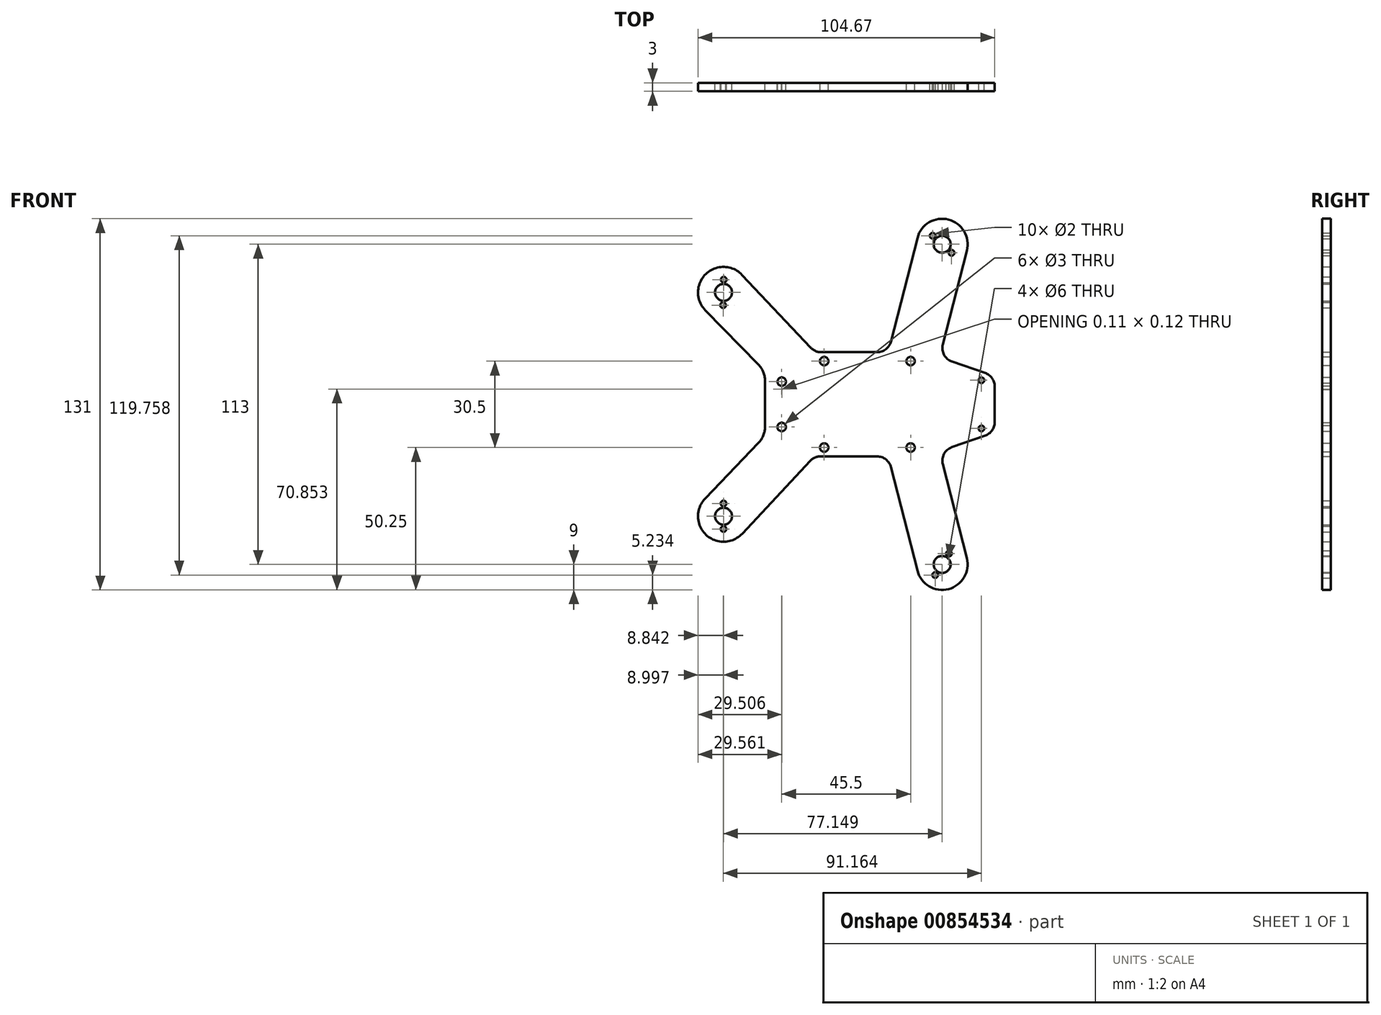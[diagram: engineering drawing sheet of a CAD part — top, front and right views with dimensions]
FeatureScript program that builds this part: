
annotation { "Feature Type Name" : "Feature", "Feature Type Description" : "" }
export const myFeature = defineFeature(function(context is Context, id is Id, definition is map)
    precondition{}
    {
        {
            var Q0;
            Q0=qCreatedBy(makeId("Front.planeOp"),FACE);
            var sketch = newSketch(context, id + "F0", { "sketchPlane" : qUnion([Q0])});
            skLineSegment(sketch, "E0.bottom", {"start": v(-3.88, -18.39) * mm, "end": v(-23.86, -18.39) * mm});
            skLineSegment(sketch, "E0.top", {"start": v(-3.88, 18.39) * mm, "end": v(-23.64, 18.39) * mm});
            skLineSegment(sketch, "E0.left", {"start": v(37.58, -6.33) * mm, "end": v(37.58, -5.89) * mm});
            skLineSegment(sketch, "E0.right", {"start": v(-37.58, -5.3) * mm, "end": v(-37.58, 5.3) * mm});
            skPoint(sketch, "E0.middle", {"position": v(0, 0) * mm});
            skPoint(sketch, "E1", {"position": v(-22.58, 15.25) * mm});
            skPoint(sketch, "E2", {"position": v(-22.58, -15.25) * mm});
            skPoint(sketch, "E3", {"position": v(7.92, 15.25) * mm});
            skPoint(sketch, "E4", {"position": v(7.92, -15.25) * mm});
            skPoint(sketch, "E5", {"position": v(32.92, 8.5) * mm});
            skPoint(sketch, "E6", {"position": v(32.92, -8.5) * mm});
            skCircle(sketch, "E7", {"center": v(-22.58, 15.25) * mm, "radius": 1.5 * mm});
            skCircle(sketch, "E8", {"center": v(-22.58, -15.25) * mm, "radius": 1.5 * mm});
            skCircle(sketch, "E9", {"center": v(7.92, 15.25) * mm, "radius": 1.5 * mm});
            skCircle(sketch, "E10", {"center": v(7.92, -15.25) * mm, "radius": 1.5 * mm});
            skCircle(sketch, "E11", {"center": v(32.92, 8.5) * mm, "radius": 1 * mm});
            skCircle(sketch, "E12", {"center": v(32.92, -8.5) * mm, "radius": 1 * mm});
            skArc(sketch, "E13", {"start": v(-37.47, 5.41) * mm, "mid": v(-37.53, 5.35) * mm, "end": v(-37.58, 5.3) * mm});
            skLineSegment(sketch, "E14", {"start": v(-37.47, 5.41) * mm, "end": v(-37.58, 5.3) * mm});
            skPoint(sketch, "E15.orphan", {"position": v(-37.58, 18.39) * mm});
            skPoint(sketch, "E16.orphan", {"position": v(-37.58, -18.39) * mm});
            skPoint(sketch, "E17", {"position": v(37.58, -9.89) * mm});
            skPoint(sketch, "E18", {"position": v(37.58, 9.89) * mm});
            skLineSegment(sketch, "E19", {"start": v(22.48, 15.14) * mm, "end": v(34.23, 11.05) * mm});
            skLineSegment(sketch, "E20", {"start": v(22.48, -15.14) * mm, "end": v(34.23, -11.05) * mm});
            skPoint(sketch, "E21.orphan", {"position": v(37.58, 18.39) * mm});
            skPoint(sketch, "E22.orphan", {"position": v(37.58, -18.39) * mm});
            skPoint(sketch, "E23", {"position": v(37.58, 5.89) * mm});
            skPoint(sketch, "E24", {"position": v(37.58, -5.89) * mm});
            skLineSegment(sketch, "E25.trimOffspring", {"start": v(37.58, 5.89) * mm, "end": v(37.58, 6.33) * mm});
            skPoint(sketch, "E26", {"position": v(-58.1, 39.5) * mm});
            skPoint(sketch, "E27", {"position": v(-58.1, -39.5) * mm});
            skPoint(sketch, "E28", {"position": v(19.06, -56.5) * mm});
            skPoint(sketch, "E29", {"position": v(19.06, 56.5) * mm});
            skPoint(sketch, "E30.center.orphan", {"position": v(-19.86, 0) * mm});
            skPoint(sketch, "E31.center.orphan", {"position": v(23.9, 0) * mm});
            skLineSegment(sketch, "E32", {"start": v(37.58, 5.89) * mm, "end": v(37.58, -5.89) * mm});
            skCircle(sketch, "E33", {"center": v(-58.1, -39.5) * mm, "radius": 3 * mm});
            skCircle(sketch, "E34", {"center": v(-58.1, 39.5) * mm, "radius": 3 * mm});
            skCircle(sketch, "E35", {"center": v(19.06, 56.5) * mm, "radius": 3 * mm});
            skCircle(sketch, "E36", {"center": v(19.06, -56.5) * mm, "radius": 3 * mm});
            skArc(sketch, "E37", {"start": v(-64.59, -33.27) * mm, "mid": v(-64.28, -46.03) * mm, "end": v(-51.52, -45.65) * mm});
            skArc(sketch, "E38", {"start": v(10.34, -58.73) * mm, "mid": v(21.29, -65.22) * mm, "end": v(27.77, -54.27) * mm});
            skArc(sketch, "E39", {"start": v(-51.55, 45.68) * mm, "mid": v(-64.33, 46) * mm, "end": v(-64.53, 33.21) * mm});
            skArc(sketch, "E40", {"start": v(27.77, 54.27) * mm, "mid": v(21.29, 65.22) * mm, "end": v(10.34, 58.73) * mm});
            skLineSegment(sketch, "E41", {"start": v(-45.75, 13.98) * mm, "end": v(-64.53, 33.21) * mm});
            skLineSegment(sketch, "E42", {"start": v(-27.27, 19.96) * mm, "end": v(-51.55, 45.68) * mm});
            skLineSegment(sketch, "E43", {"start": v(-27.52, -19.97) * mm, "end": v(-51.52, -45.65) * mm});
            skLineSegment(sketch, "E44", {"start": v(-45.7, -13.58) * mm, "end": v(-64.59, -33.27) * mm});
            skLineSegment(sketch, "E45", {"start": v(27.77, 54.27) * mm, "end": v(19.28, 21.1) * mm});
            skLineSegment(sketch, "E46", {"start": v(19.28, -21.1) * mm, "end": v(27.77, -54.27) * mm});
            skLineSegment(sketch, "E47", {"start": v(0.96, -22.15) * mm, "end": v(10.34, -58.73) * mm});
            skLineSegment(sketch, "E48", {"start": v(0.96, 22.15) * mm, "end": v(10.34, 58.73) * mm});
            skLineSegment(sketch, "E49", {"start": v(-43.47, 8.4) * mm, "end": v(-43.47, -8.04) * mm});
            skPoint(sketch, "E50.newPointA", {"position": v(13.14, -18.39) * mm});
            skPoint(sketch, "E50.newPointB", {"position": v(0, -18.39) * mm});
            skArc(sketch, "E50.filletArc", {"start": v(0.96, -22.15) * mm, "mid": v(-0.81, -19.44) * mm, "end": v(-3.88, -18.39) * mm});
            skPoint(sketch, "E51.newPointA", {"position": v(0, 18.39) * mm});
            skPoint(sketch, "E51.newPointB", {"position": v(13.14, 18.39) * mm});
            skArc(sketch, "E51.filletArc", {"start": v(-3.88, 18.39) * mm, "mid": v(-0.81, 19.44) * mm, "end": v(0.96, 22.15) * mm});
            skPoint(sketch, "E52.visualSharp", {"position": v(-25.8, 18.39) * mm});
            skArc(sketch, "E52.filletArc", {"start": v(-27.27, 19.96) * mm, "mid": v(-25.62, 18.8) * mm, "end": v(-23.64, 18.39) * mm});
            skPoint(sketch, "E53.visualSharp", {"position": v(-26.03, -18.39) * mm});
            skArc(sketch, "E53.filletArc", {"start": v(-23.86, -18.39) * mm, "mid": v(-25.85, -18.8) * mm, "end": v(-27.52, -19.97) * mm});
            skArc(sketch, "E54.filletArc", {"start": v(-45.7, -13.58) * mm, "mid": v(-44.05, -11.02) * mm, "end": v(-43.47, -8.04) * mm});
            skArc(sketch, "E55.filletArc", {"start": v(-43.47, 8.4) * mm, "mid": v(-44.06, 11.41) * mm, "end": v(-45.75, 13.98) * mm});
            skPoint(sketch, "E56.newPointA", {"position": v(18.14, 16.65) * mm});
            skArc(sketch, "E56.filletArc", {"start": v(19.28, 21.1) * mm, "mid": v(19.72, 17.5) * mm, "end": v(22.48, 15.14) * mm});
            skPoint(sketch, "E57.newPointB", {"position": v(18.14, -16.65) * mm});
            skArc(sketch, "E57.filletArc", {"start": v(22.48, -15.14) * mm, "mid": v(19.72, -17.5) * mm, "end": v(19.28, -21.1) * mm});
            skArc(sketch, "E58.filletArc", {"start": v(34.23, -11.05) * mm, "mid": v(36.66, -9.23) * mm, "end": v(37.58, -6.33) * mm});
            skArc(sketch, "E59.filletArc", {"start": v(37.58, 6.33) * mm, "mid": v(36.66, 9.23) * mm, "end": v(34.23, 11.05) * mm});
            skLineSegment(sketch, "E60", {"start": v(-37.56, 8) * mm, "end": v(-37.56, 0) * mm});
            skLineSegment(sketch, "E61", {"start": v(-37.56, 0) * mm, "end": v(-37.58, -8) * mm});
            skCircle(sketch, "E62", {"center": v(-37.56, 8) * mm, "radius": 1.5 * mm});
            skCircle(sketch, "E63", {"center": v(-37.58, -8) * mm, "radius": 1.5 * mm});
            skCircle(sketch, "E64", {"center": v(-58.02, 44) * mm, "radius": 1 * mm});
            skCircle(sketch, "E65", {"center": v(-58.25, 35) * mm, "radius": 1 * mm});
            skCircle(sketch, "E66", {"center": v(-58.1, -35) * mm, "radius": 1 * mm});
            skCircle(sketch, "E67", {"center": v(-58.1, -44) * mm, "radius": 1 * mm});
            skCircle(sketch, "E68", {"center": v(15.7, 59.5) * mm, "radius": 1 * mm});
            skCircle(sketch, "E69", {"center": v(22.38, 53.47) * mm, "radius": 1 * mm});
            skCircle(sketch, "E70", {"center": v(16.6, -60.27) * mm, "radius": 1 * mm});
            skCircle(sketch, "E71", {"center": v(21.45, -52.69) * mm, "radius": 1 * mm});
            skSolve(sketch);
        }
        {
            var Q0;
            Q0=makeQuery(id+"F0.imprint","IMPRINT",FACE,{"disambiguationData":[TD([[makeQuery(id+"F0.imprint","IMPRINT",EDGE,{"derivedFrom":sQuery(id+"F0.wireOp",EDGE,"E0.bottom")}),-1.0]])]});
            extrude(context, id + "F1", {"entities" : qUnion([Q0]), "depth" : 3 * mm, "offsetDistance" : 25 * mm});
        }
    });
